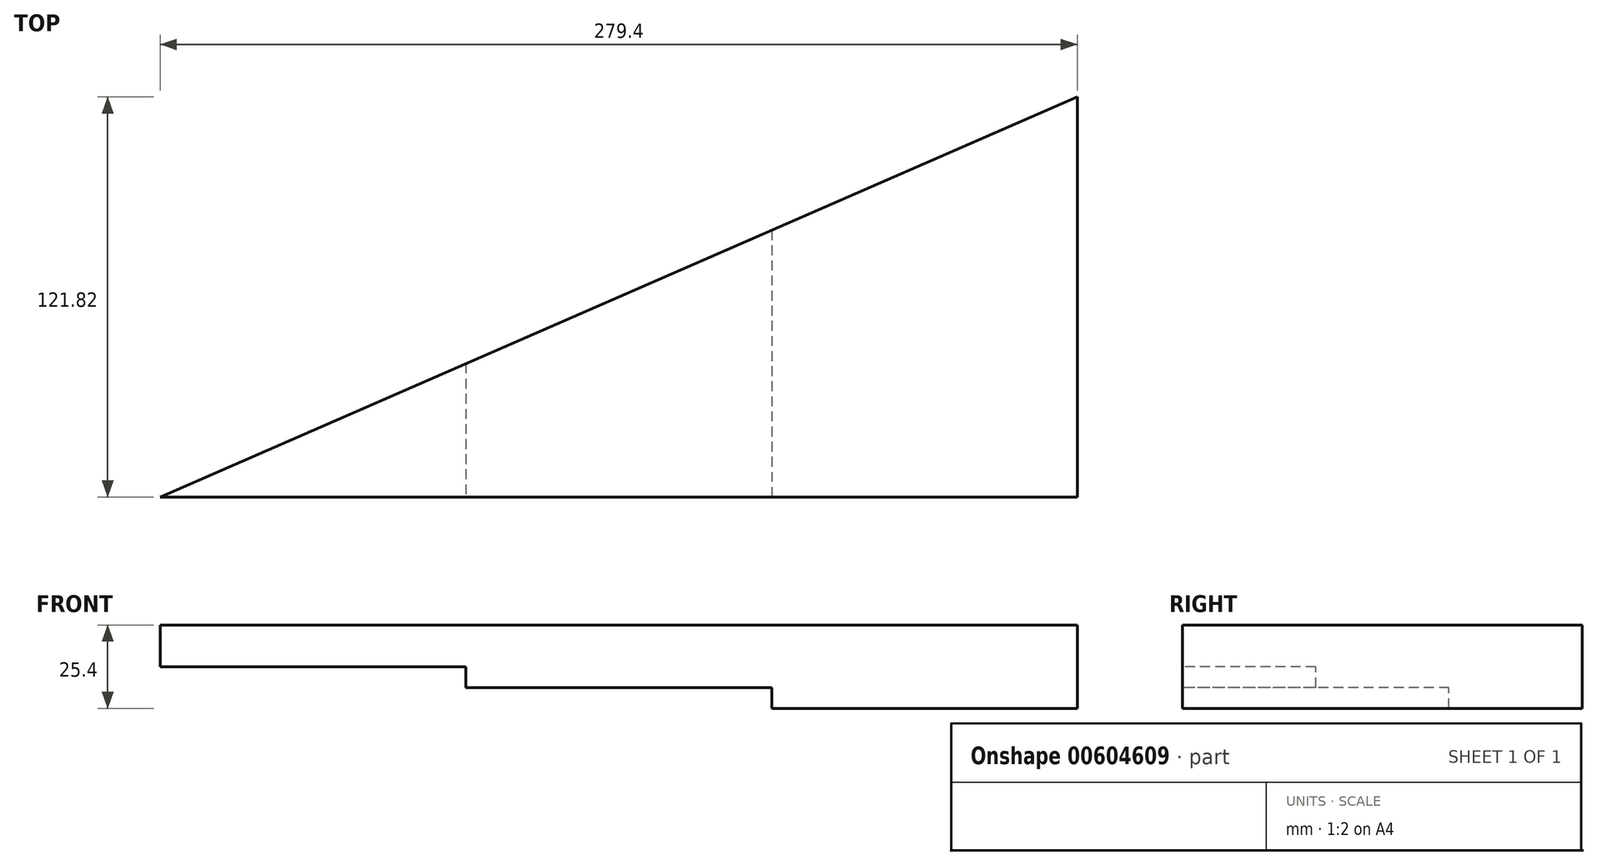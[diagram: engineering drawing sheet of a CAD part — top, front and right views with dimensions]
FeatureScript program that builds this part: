
annotation { "Feature Type Name" : "Feature", "Feature Type Description" : "" }
export const myFeature = defineFeature(function(context is Context, id is Id, definition is map)
    precondition{}
    {
        {
            var Q0;
            Q0=qCreatedBy(makeId("Top.planeOp"),FACE);
            var sketch = newSketch(context, id + "F0", { "sketchPlane" : qUnion([Q0])});
            skLineSegment(sketch, "E0", {"start": v(-115.05, -42.88) * mm, "end": v(164.35, -42.88) * mm});
            skLineSegment(sketch, "E1", {"start": v(164.35, -42.88) * mm, "end": v(164.35, 78.94) * mm});
            skLineSegment(sketch, "E2", {"start": v(164.35, 78.94) * mm, "end": v(-115.05, -42.88) * mm});
            skSolve(sketch);
        }
        {
            var Q0;
            Q0 = qSketchRegion(id + "F0", true);
            var sketch = newSketch(context, id + "F1", { "sketchPlane" : qUnion([Q0])});
            skLineSegment(sketch, "E3.0", {"start": v(164.35, 78.94) * mm, "end": v(71.22, 38.33) * mm});
            skLineSegment(sketch, "E4.0", {"start": v(164.35, -42.88) * mm, "end": v(164.35, 78.94) * mm});
            skLineSegment(sketch, "E5", {"start": v(-21.91, -2.27) * mm, "end": v(-115.05, -42.88) * mm});
            skLineSegment(sketch, "E6", {"start": v(71.22, 38.33) * mm, "end": v(-21.91, -2.27) * mm});
            skLineSegment(sketch, "E7.0", {"start": v(-115.05, -42.88) * mm, "end": v(-21.91, -42.88) * mm});
            skLineSegment(sketch, "E8", {"start": v(71.22, 38.33) * mm, "end": v(71.22, -42.88) * mm});
            skLineSegment(sketch, "E9", {"start": v(-21.91, -2.27) * mm, "end": v(-21.91, -42.88) * mm});
            skLineSegment(sketch, "E10", {"start": v(-21.91, -42.88) * mm, "end": v(71.22, -42.88) * mm});
            skLineSegment(sketch, "E11", {"start": v(71.22, -42.88) * mm, "end": v(164.35, -42.88) * mm});
            skSolve(sketch);
        }
        {
            var Q0;
            Q0=makeQuery(id+"F0.imprint","IMPRINT",FACE,{"disambiguationData":[TD([[makeQuery(id+"F0.imprint","IMPRINT",EDGE,{"derivedFrom":sQuery(id+"F0.wireOp",EDGE,"E0")}),1.0]])]});
            extrude(context, id + "F2", {"entities" : qUnion([Q0]), "depth" : 6.35 * mm, "offsetDistance" : 25.4 * mm});
        }
        {
            var Q0;
            {var subQ0=sQuery(id+"F1.wireOp",EDGE,"E5");Q0=makeQuery(id+"F1.imprint","IMPRINT",FACE,{"disambiguationData":[TD([[makeQuery(id+"F1.imprint","IMPRINT",EDGE,{"derivedFrom":subQ0}),1.0]])]});}
            extrude(context, id + "F3", {"entities" : qUnion([Q0]), "oppositeDirection" : true, "depth" : 6.35 * mm, "offsetDistance" : 25.4 * mm});
        }
        {
            var Q0;
            Q0=makeQuery(id+"F1.imprint","IMPRINT",FACE,{"disambiguationData":[TD([[makeQuery(id+"F1.imprint","IMPRINT",EDGE,{"derivedFrom":sQuery(id+"F1.wireOp",EDGE,"E6")}),1.0]])]});
            extrude(context, id + "F4", {"entities" : qUnion([Q0]), "operationType" : NewBodyOperationType.ADD, "oppositeDirection" : true, "depth" : 12.7 * mm, "offsetDistance" : 25.4 * mm});
        }
        {
            var Q0;
            Q0=makeQuery(id+"F1.imprint","IMPRINT",FACE,{"disambiguationData":[TD([[makeQuery(id+"F1.imprint","IMPRINT",EDGE,{"derivedFrom":sQuery(id+"F1.wireOp",EDGE,"E3.0")}),1.0]])]});
            extrude(context, id + "F5", {"entities" : qUnion([Q0]), "operationType" : NewBodyOperationType.ADD, "oppositeDirection" : true, "depth" : 19.05 * mm, "offsetDistance" : 25.4 * mm});
        }
    });
